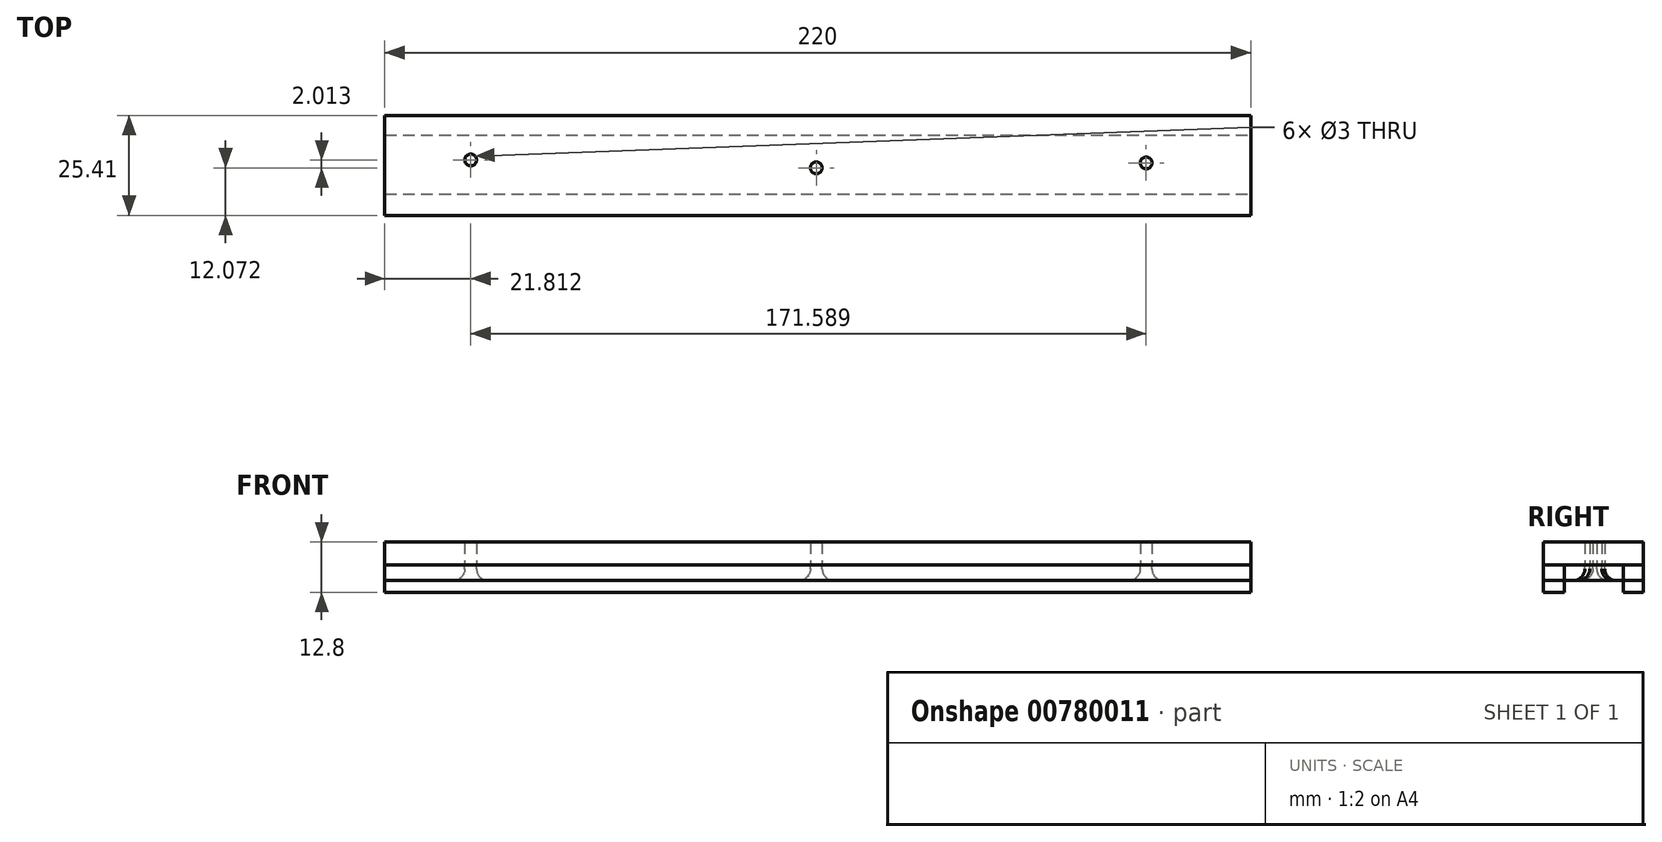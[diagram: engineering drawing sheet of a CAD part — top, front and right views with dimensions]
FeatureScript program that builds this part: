
annotation { "Feature Type Name" : "Feature", "Feature Type Description" : "" }
export const myFeature = defineFeature(function(context is Context, id is Id, definition is map)
    precondition{}
    {
        {
            var Q0;
            Q0=qCreatedBy(makeId("Top.planeOp"),FACE);
            var sketch = newSketch(context, id + "F0", { "sketchPlane" : qUnion([Q0])});
            skLineSegment(sketch, "E0.bottom", {"start": v(-109.62, 3.15) * mm, "end": v(110.38, 3.15) * mm});
            skLineSegment(sketch, "E0.top", {"start": v(-109.62, -11.85) * mm, "end": v(110.38, -11.85) * mm});
            skLineSegment(sketch, "E0.left", {"start": v(-109.62, 3.15) * mm, "end": v(-109.62, -11.85) * mm});
            skLineSegment(sketch, "E0.right", {"start": v(110.38, 3.15) * mm, "end": v(110.38, -11.85) * mm});
            skLineSegment(sketch, "E1.top", {"start": v(-109.62, 8.18) * mm, "end": v(110.38, 8.18) * mm});
            skLineSegment(sketch, "E1.left", {"start": v(-109.62, 3.15) * mm, "end": v(-109.62, 8.18) * mm});
            skLineSegment(sketch, "E1.right", {"start": v(110.38, 3.15) * mm, "end": v(110.38, 8.18) * mm});
            skLineSegment(sketch, "E2.top", {"start": v(-109.62, -17.23) * mm, "end": v(110.38, -17.23) * mm});
            skLineSegment(sketch, "E2.left", {"start": v(-109.62, -11.85) * mm, "end": v(-109.62, -17.23) * mm});
            skLineSegment(sketch, "E2.right", {"start": v(110.38, -11.85) * mm, "end": v(110.38, -17.23) * mm});
            skCircle(sketch, "E3", {"center": v(-87.8, -3.14) * mm, "radius": 1.5 * mm});
            skCircle(sketch, "E4", {"center": v(83.78, -3.9) * mm, "radius": 1.5 * mm});
            skCircle(sketch, "E5", {"center": v(0, -5.16) * mm, "radius": 1.5 * mm});
            skSolve(sketch);
        }
        {
            var Q0;
            Q0=makeQuery(id+"F0.imprint","IMPRINT",FACE,{"disambiguationData":[TD([[makeQuery(id+"F0.imprint","IMPRINT",EDGE,{"derivedFrom":sQuery(id+"F0.wireOp",EDGE,"E0.top")}),-1.0]])]});
            var Q1;
            Q1=makeQuery(id+"F0.imprint","IMPRINT",FACE,{"disambiguationData":[TD([[makeQuery(id+"F0.imprint","IMPRINT",EDGE,{"derivedFrom":sQuery(id+"F0.wireOp",EDGE,"E0.bottom")}),1.0]])]});
            extrude(context, id + "F1", {"entities" : qUnion([Q0, Q1]), "oppositeDirection" : true, "depth" : 7 * mm, "offsetDistance" : 25 * mm});
        }
        {
            var Q0;
            Q0 = qSketchRegion(id + "F0", true);
            extrude(context, id + "F2", {"entities" : qUnion([Q0]), "depth" : 5.8 * mm, "offsetDistance" : 25 * mm});
        }
        {
            var Q0;
            Q0 = qSketchRegion(id + "F0", true);
            extrude(context, id + "F3", {"entities" : qUnion([Q0]), "oppositeDirection" : true, "depth" : 4 * mm, "offsetDistance" : 25 * mm});
        }
        {
            var Q0;
            Q0=makeQuery(id+"F3.opExtrude","CAP_EDGE",EDGE,{"disambiguationData":[OSD([sQuery(id+"F0.wireOp",EDGE,"E3")])],"isStart":false});
            var Q1;
            Q1=makeQuery(id+"F3.opExtrude","CAP_EDGE",EDGE,{"disambiguationData":[OSD([sQuery(id+"F0.wireOp",EDGE,"E4")])],"isStart":false});
            var Q2;
            Q2=makeQuery(id+"F3.opExtrude","CAP_EDGE",EDGE,{"disambiguationData":[OSD([sQuery(id+"F0.wireOp",EDGE,"E5")])],"isStart":false});
            fillet(context, id + "F4", {"entities" : qUnion([Q0, Q1, Q2]), "radius" : 3 * mm, "tangentPropagation" : true, "allowEdgeOverflow" : false});
        }
    });
